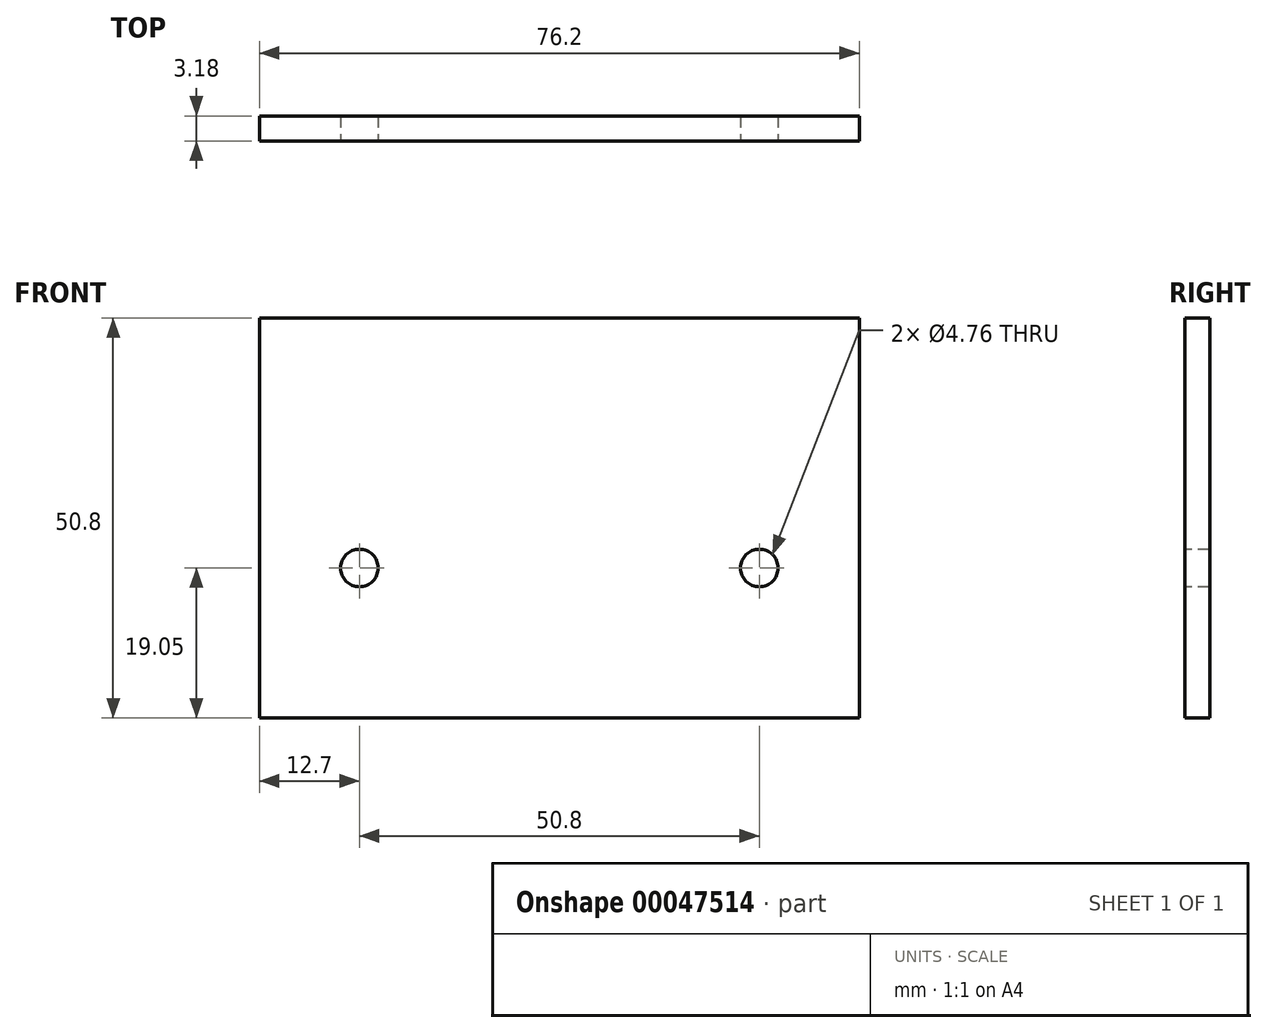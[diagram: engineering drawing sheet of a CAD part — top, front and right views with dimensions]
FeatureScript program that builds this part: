
annotation { "Feature Type Name" : "Feature", "Feature Type Description" : "" }
export const myFeature = defineFeature(function(context is Context, id is Id, definition is map)
    precondition{}
    {
        {
            var Q0;
            Q0=qCreatedBy(makeId("Front.planeOp"),FACE);
            var sketch = newSketch(context, id + "F0", { "sketchPlane" : qUnion([Q0])});
            skLineSegment(sketch, "E0.rect.bottom", {"start": v(-38.1, 25.4) * mm, "end": v(38.1, 25.4) * mm});
            skLineSegment(sketch, "E0.rect.top", {"start": v(-38.1, -25.4) * mm, "end": v(38.1, -25.4) * mm});
            skLineSegment(sketch, "E0.rect.left", {"start": v(-38.1, 25.4) * mm, "end": v(-38.1, -25.4) * mm});
            skLineSegment(sketch, "E0.rect.right", {"start": v(38.1, 25.4) * mm, "end": v(38.1, -25.4) * mm});
            skPoint(sketch, "E0.rect.middle", {"position": v(0, 0) * mm});
            skSolve(sketch);
        }
        {
            var Q0;
            Q0=makeQuery(id+"F0.imprint","IMPRINT",FACE,{"disambiguationData":[TD([[makeQuery(id+"F0.imprint","IMPRINT",EDGE,{"derivedFrom":sQuery(id+"F0.wireOp",EDGE,"E0.rect.bottom")}),-1.0]])]});
            extrude(context, id + "F1", {"entities" : qUnion([Q0]), "endBound" : BoundingType.SYMMETRIC, "depth" : 3.17 * mm});
        }
        {
            var Q0;
            Q0=makeQuery(id+"F1.opExtrude","CAP_FACE",FACE,{"disambiguationData":[OSD([sQuery(id+"F0.wireOp",EDGE,"E0.rect.bottom"),sQuery(id+"F0.wireOp",EDGE,"E0.rect.top"),sQuery(id+"F0.wireOp",EDGE,"E0.rect.left"),sQuery(id+"F0.wireOp",EDGE,"E0.rect.right")])],"isStart":false});
            var sketch = newSketch(context, id + "F2", { "sketchPlane" : qUnion([Q0])});
            skCircle(sketch, "E1", {"center": v(-25.4, -6.35) * mm, "radius": 2.38 * mm});
            skSolve(sketch);
        }
        {
            var Q0;
            Q0=makeQuery(id+"F2.imprint","IMPRINT",FACE,{"disambiguationData":[TD([[makeQuery(id+"F2.imprint","IMPRINT",EDGE,{"derivedFrom":sQuery(id+"F2.wireOp",EDGE,"E1")}),-1.0]])]});
            var sketch = newSketch(context, id + "F3", { "sketchPlane" : qUnion([Q0])});
            skCircle(sketch, "E2", {"center": v(25.4, -6.35) * mm, "radius": 2.38 * mm});
            skSolve(sketch);
        }
        {
            var Q0;
            Q0=makeQuery(id+"F2.imprint","IMPRINT",FACE,{"disambiguationData":[TD([[makeQuery(id+"F2.imprint","IMPRINT",EDGE,{"derivedFrom":sQuery(id+"F2.wireOp",EDGE,"E1")}),1.0]])]});
            extrude(context, id + "F4", {"entities" : qUnion([Q0]), "operationType" : NewBodyOperationType.REMOVE, "oppositeDirection" : true, "depth" : 3.17 * mm});
        }
        {
            var Q0;
            Q0=makeQuery(id+"F3.imprint","IMPRINT",FACE,{"disambiguationData":[TD([[makeQuery(id+"F3.imprint","IMPRINT",EDGE,{"derivedFrom":sQuery(id+"F3.wireOp",EDGE,"E2")}),1.0]])]});
            extrude(context, id + "F5", {"entities" : qUnion([Q0]), "operationType" : NewBodyOperationType.REMOVE, "oppositeDirection" : true, "depth" : 3.17 * mm});
        }
    });
